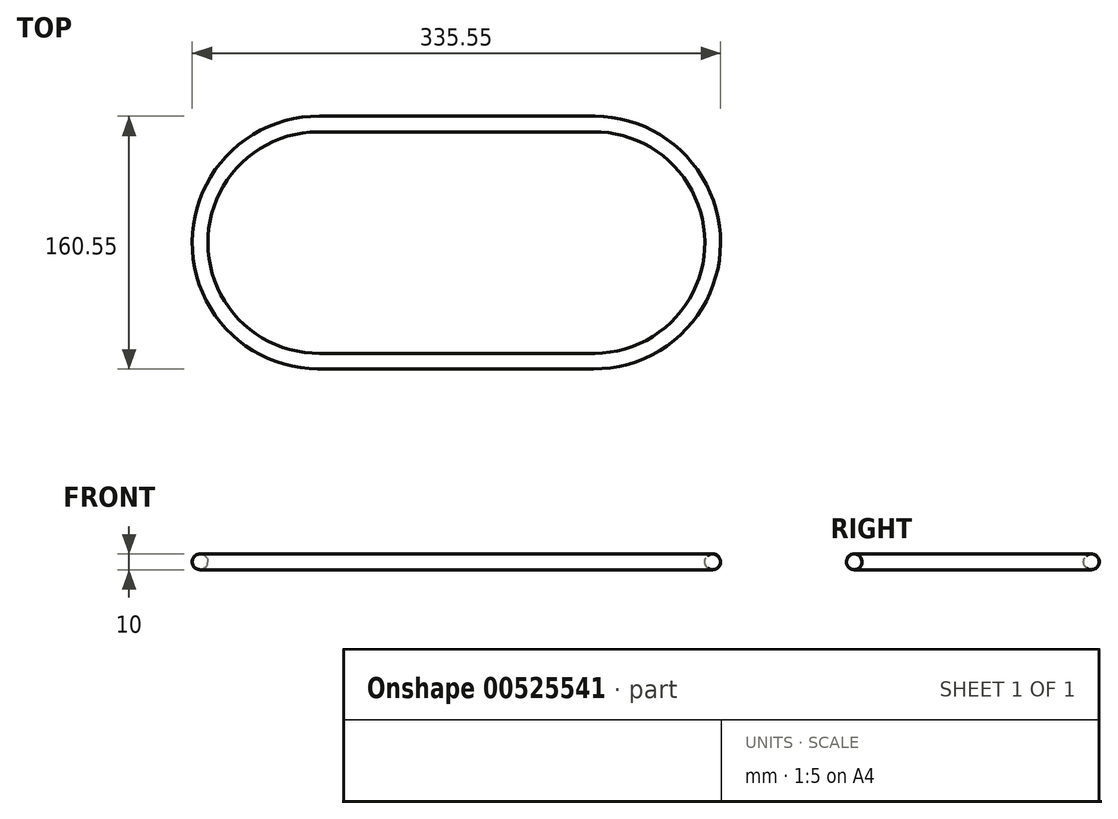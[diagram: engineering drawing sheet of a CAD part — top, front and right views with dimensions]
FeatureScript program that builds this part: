
annotation { "Feature Type Name" : "Feature", "Feature Type Description" : "" }
export const myFeature = defineFeature(function(context is Context, id is Id, definition is map)
    precondition{}
    {
        {
            var Q0;
            Q0=qCreatedBy(makeId("Top.planeOp"),FACE);
            var sketch = newSketch(context, id + "F0", { "sketchPlane" : qUnion([Q0])});
            skLineSegment(sketch, "E0.bottom", {"start": v(-182.53, 185.72) * mm, "end": v(-7.53, 185.72) * mm});
            skLineSegment(sketch, "E0.top", {"start": v(-182.53, 35.72) * mm, "end": v(-7.53, 35.72) * mm});
            skLineSegment(sketch, "E0.left", {"start": v(-257.53, 110.72) * mm, "end": v(-257.53, 110.72) * mm});
            skLineSegment(sketch, "E0.right", {"start": v(67.47, 110.72) * mm, "end": v(67.47, 110.72) * mm});
            skPoint(sketch, "E1.visualSharp", {"position": v(-257.53, 185.72) * mm});
            skArc(sketch, "E1.filletArc", {"start": v(-182.53, 185.72) * mm, "mid": v(-235.57, 163.75) * mm, "end": v(-257.53, 110.72) * mm});
            skPoint(sketch, "E2.visualSharp", {"position": v(-257.53, 35.72) * mm});
            skArc(sketch, "E2.filletArc", {"start": v(-257.53, 110.72) * mm, "mid": v(-235.57, 57.68) * mm, "end": v(-182.53, 35.72) * mm});
            skPoint(sketch, "E3.visualSharp", {"position": v(67.47, 185.72) * mm});
            skArc(sketch, "E3.filletArc", {"start": v(67.47, 110.72) * mm, "mid": v(45.5, 163.75) * mm, "end": v(-7.53, 185.72) * mm});
            skPoint(sketch, "E4.visualSharp", {"position": v(67.47, 35.72) * mm});
            skArc(sketch, "E4.filletArc", {"start": v(-7.53, 35.72) * mm, "mid": v(45.5, 57.68) * mm, "end": v(67.47, 110.72) * mm});
            skSolve(sketch);
        }
        {
            var Q0;
            Q0=qCreatedBy(makeId("Right.planeOp"),FACE);
            var sketch = newSketch(context, id + "F1", { "sketchPlane" : qUnion([Q0])});
            skCircle(sketch, "E5", {"center": v(35.8, 0) * mm, "radius": 5 * mm});
            skSolve(sketch);
        }
        {
            var Q0;
            Q0=makeQuery(id+"F1.imprint","IMPRINT",FACE,{"disambiguationData":[TD([[makeQuery(id+"F1.imprint","IMPRINT",EDGE,{"derivedFrom":sQuery(id+"F1.wireOp",EDGE,"E5")}),1.0]])]});
            var Q1;
            Q1 = qConstructionFilter(qBodyType(qCreatedBy(id + "F0" ,EDGE), BodyType.WIRE), ConstructionObject.NO);
            sweep(context, id + "F2", {"profiles" : qUnion([Q0]), "path" : qUnion([Q1])});
        }
    });
